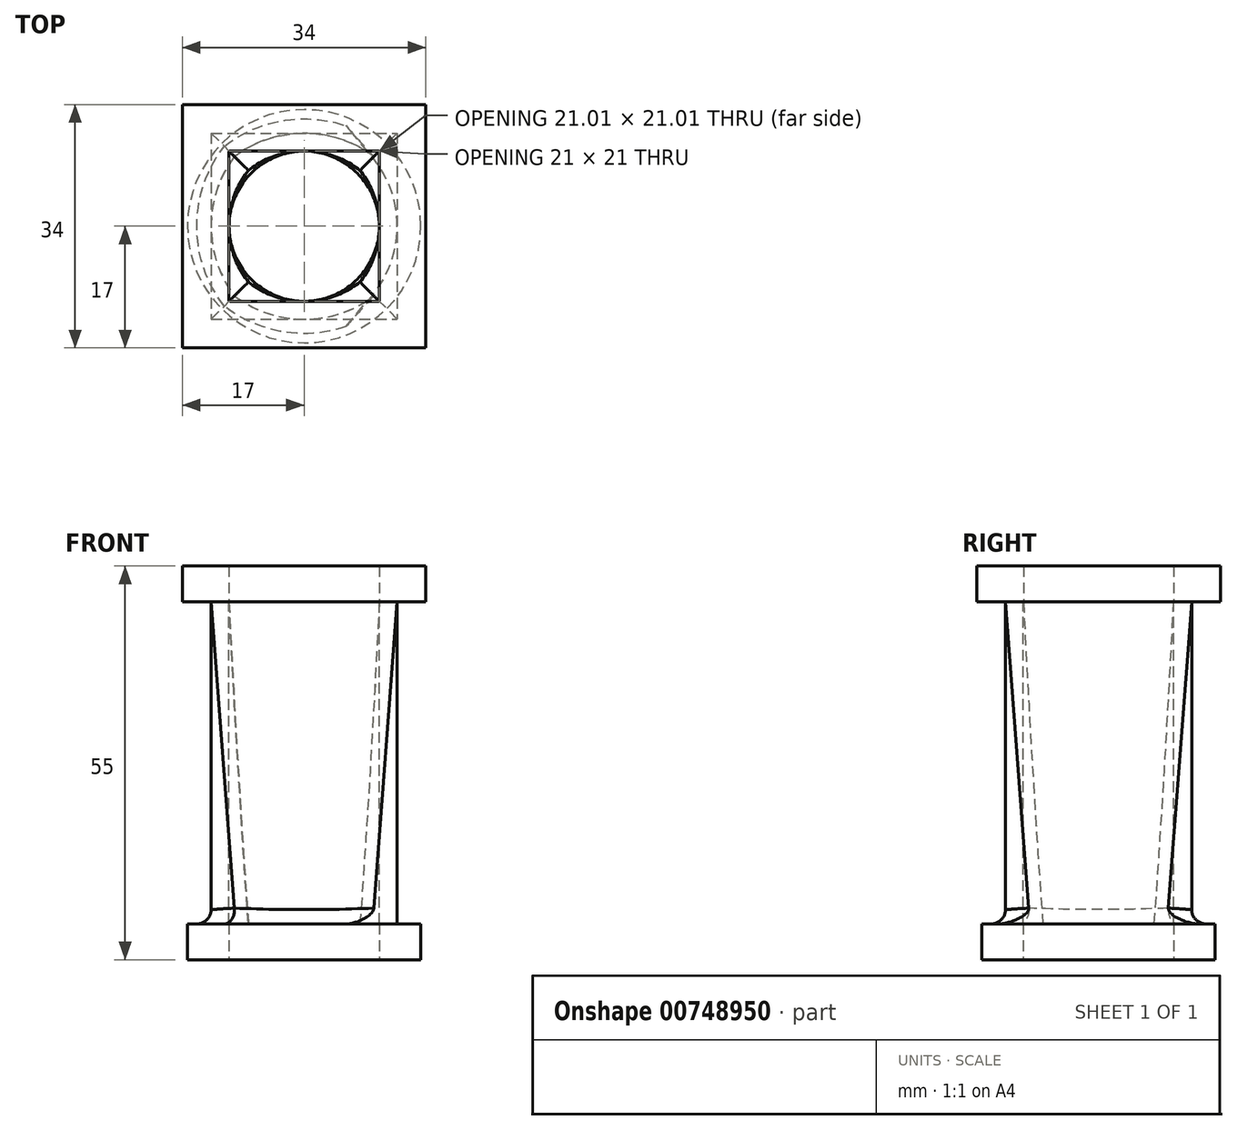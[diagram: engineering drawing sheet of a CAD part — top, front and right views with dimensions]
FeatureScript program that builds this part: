
annotation { "Feature Type Name" : "Feature", "Feature Type Description" : "" }
export const myFeature = defineFeature(function(context is Context, id is Id, definition is map)
    precondition{}
    {
        {
            var Q0;
            Q0=qCreatedBy(makeId("Top.planeOp"),FACE);
            var sketch = newSketch(context, id + "F0", { "sketchPlane" : qUnion([Q0])});
            skCircle(sketch, "E0", {"center": v(0, 0) * mm, "radius": 25 * mm});
            skCircle(sketch, "E1", {"center": v(0, 18) * mm, "radius": 2.5 * mm, "construction": true});
            skCircle(sketch, "E2", {"center": v(0, 0) * mm, "radius": 20.5 * mm});
            skCircle(sketch, "E3.1.0", {"center": v(-15.59, -9) * mm, "radius": 2.5 * mm, "construction": true});
            skCircle(sketch, "E3.2.0", {"center": v(15.59, -9) * mm, "radius": 2.5 * mm, "construction": true});
            skCircle(sketch, "E4", {"center": v(0, 0) * mm, "radius": 13 * mm});
            skSolve(sketch);
        }
        {
            var Q0;
            Q0=qCreatedBy(makeId("Top.planeOp"),FACE);
            cPlane(context, id + "F1", {"entities" : qUnion([Q0]), "cplaneType" : CPlaneType.OFFSET, "offset" : 50 * mm, "width" : 150 * mm, "height" : 150 * mm});
        }
        {
            var Q0;
            Q0=qCreatedBy(id+"F1.planeOp",FACE);
            var sketch = newSketch(context, id + "F2", { "sketchPlane" : qUnion([Q0])});
            skLineSegment(sketch, "E5.bottom", {"start": v(25, 25) * mm, "end": v(-25, 25) * mm});
            skLineSegment(sketch, "E5.top", {"start": v(25, -25) * mm, "end": v(-25, -25) * mm});
            skLineSegment(sketch, "E5.left", {"start": v(25, 25) * mm, "end": v(25, -25) * mm});
            skLineSegment(sketch, "E5.right", {"start": v(-25, 25) * mm, "end": v(-25, -25) * mm});
            skPoint(sketch, "E5.middle", {"position": v(0, 0) * mm});
            skPoint(sketch, "E6", {"position": v(0, 25) * mm});
            skLineSegment(sketch, "E7.bottom", {"start": v(18, 18) * mm, "end": v(-18, 18) * mm});
            skLineSegment(sketch, "E7.top", {"start": v(18, -18) * mm, "end": v(-18, -18) * mm});
            skLineSegment(sketch, "E7.left", {"start": v(18, 18) * mm, "end": v(18, -18) * mm});
            skLineSegment(sketch, "E7.right", {"start": v(-18, 18) * mm, "end": v(-18, -18) * mm});
            skLineSegment(sketch, "E8.bottom", {"start": v(-13, 13) * mm, "end": v(13, 13) * mm});
            skLineSegment(sketch, "E8.top", {"start": v(-13, -13) * mm, "end": v(13, -13) * mm});
            skLineSegment(sketch, "E8.left", {"start": v(-13, 13) * mm, "end": v(-13, -13) * mm});
            skLineSegment(sketch, "E8.right", {"start": v(13, 13) * mm, "end": v(13, -13) * mm});
            skSolve(sketch);
        }
        {
            var Q0;
            Q0=makeQuery(id+"F2.imprint","IMPRINT",FACE,{"disambiguationData":[TD([[makeQuery(id+"F2.imprint","IMPRINT",EDGE,{"derivedFrom":sQuery(id+"F2.wireOp",EDGE,"E8.bottom")}),-1.0]])]});
            var Q1;
            Q1=makeQuery(id+"F0.imprint","IMPRINT",FACE,{"disambiguationData":[TD([[makeQuery(id+"F0.imprint","IMPRINT",EDGE,{"derivedFrom":sQuery(id+"F0.wireOp",EDGE,"E4")}),1.0]])]});
            loft(context, id + "F3", {"sheetProfilesArray" : [{ "sheetProfileEntities" : qUnion([Q0]) }, { "sheetProfileEntities" : qUnion([Q1]) }]});
        }
        {
            var Q0;
            Q0=makeQuery(id+"F3.opLoft","CAP_FACE",FACE,{"disambiguationData":[OSD([makeQuery(id+"F0.imprint","IMPRINT",FACE,{"disambiguationData":[TD([[makeQuery(id+"F0.imprint","IMPRINT",EDGE,{"derivedFrom":sQuery(id+"F0.wireOp",EDGE,"E4")}),1.0]])]})])],"isStart":true});
            var Q1;
            Q1=makeQuery(id+"F3.opLoft","CAP_FACE",FACE,{"disambiguationData":[OSD([makeQuery(id+"F2.imprint","IMPRINT",FACE,{"disambiguationData":[TD([[makeQuery(id+"F2.imprint","IMPRINT",EDGE,{"derivedFrom":sQuery(id+"F2.wireOp",EDGE,"E8.bottom")}),-1.0]])]})])],"isStart":true});
            shell(context, id + "F4", {"entities" : qUnion([Q0, Q1]), "thickness" : 2.5 * mm});
        }
        {
            var Q0;
            Q0=makeQuery(id+"F3.opLoft","CAP_FACE",FACE,{"disambiguationData":[OSD([makeQuery(id+"F0.imprint","IMPRINT",FACE,{"disambiguationData":[TD([[makeQuery(id+"F0.imprint","IMPRINT",EDGE,{"derivedFrom":sQuery(id+"F0.wireOp",EDGE,"E4")}),1.0]])]})])],"isStart":true});
            var sketch = newSketch(context, id + "F5", { "sketchPlane" : qUnion([Q0])});
            skCircle(sketch, "E9", {"center": v(0, 0) * mm, "radius": 16.3 * mm});
            skSolve(sketch);
        }
        {
            var Q0;
            Q0=makeQuery(id+"F5.imprint","IMPRINT",FACE,{"disambiguationData":[TD([[makeQuery(id+"F5.imprint","IMPRINT",EDGE,{"derivedFrom":sQuery(id+"F5.wireOp",EDGE,"E9")}),1.0]])]});
            var Q1;
            {var subQ2=sQuery(id+"F2.wireOp",EDGE,"E8.bottom");var subQ3=sQuery(id+"F0.wireOp",EDGE,"E4");var subQ5=sQuery(id+"F2.wireOp",EDGE,"E8.left");Q1=makeQuery(id+"F5.imprint","IMPRINT",FACE,{"disambiguationData":[TD([[makeQuery(id+"F5.imprint","IMPRINT",EDGE,{"derivedFrom":makeQuery(id+"F3.opLoft","MID_CAP_EDGE",EDGE,{"disambiguationData":[OSD([subQ3,subQ2,subQ5])],"capPos":1.0})}),1.0]])]});}
            extrude(context, id + "F6", {"entities" : qUnion([Q0, Q1]), "operationType" : NewBodyOperationType.ADD, "oppositeDirection" : true, "depth" : 5 * mm, "offsetDistance" : 25 * mm});
        }
        {
            var Q0;
            Q0=makeQuery(id+"F3.opLoft","CAP_FACE",FACE,{"disambiguationData":[OSD([makeQuery(id+"F2.imprint","IMPRINT",FACE,{"disambiguationData":[TD([[makeQuery(id+"F2.imprint","IMPRINT",EDGE,{"derivedFrom":sQuery(id+"F2.wireOp",EDGE,"E8.bottom")}),-1.0]])]})])],"isStart":true});
            var sketch = newSketch(context, id + "F7", { "sketchPlane" : qUnion([Q0])});
            skLineSegment(sketch, "E10.bottom", {"start": v(-17, 17) * mm, "end": v(17, 17) * mm});
            skLineSegment(sketch, "E10.top", {"start": v(-17, -17) * mm, "end": v(17, -17) * mm});
            skLineSegment(sketch, "E10.left", {"start": v(-17, 17) * mm, "end": v(-17, -17) * mm});
            skLineSegment(sketch, "E10.right", {"start": v(17, 17) * mm, "end": v(17, -17) * mm});
            skPoint(sketch, "E10.middle", {"position": v(0, 0) * mm});
            skSolve(sketch);
        }
        {
            var Q0;
            Q0=makeQuery(id+"F7.imprint","IMPRINT",FACE,{"disambiguationData":[TD([[makeQuery(id+"F7.imprint","IMPRINT",EDGE,{"derivedFrom":sQuery(id+"F7.wireOp",EDGE,"E10.bottom")}),-1.0]])]});
            var Q1;
            {var subQ0=sQuery(id+"F2.wireOp",EDGE,"E8.right");var subQ1=sQuery(id+"F2.wireOp",EDGE,"E8.left");var subQ3=sQuery(id+"F2.wireOp",EDGE,"E8.bottom");Q1=makeQuery(id+"F7.imprint","IMPRINT",FACE,{"disambiguationData":[TD([[makeQuery(id+"F7.imprint","IMPRINT",EDGE,{"derivedFrom":makeQuery(id+"F3.opLoft","MID_CAP_EDGE",EDGE,{"disambiguationData":[OSD([subQ3,subQ1,subQ0])],"capPos":0.0})}),-1.0]])]});}
            extrude(context, id + "F8", {"entities" : qUnion([Q0, Q1]), "depth" : 5 * mm, "offsetDistance" : 25 * mm});
        }
        {
            var Q0;
            {var subQ0=sQuery(id+"F2.wireOp",EDGE,"E8.right");var subQ1=sQuery(id+"F2.wireOp",EDGE,"E8.left");var subQ2=sQuery(id+"F2.wireOp",EDGE,"E8.top");var subQ3=sQuery(id+"F2.wireOp",EDGE,"E8.bottom");var subQ4=sQuery(id+"F0.wireOp",EDGE,"E4");Q0=makeQuery(id+"F6.boolean.opBoolean","INTERSECT",EDGE,{"derivedFrom":[makeQuery(id+"F3.opLoft","SWEPT_FACE",FACE,{"disambiguationData":[OSD([subQ4,subQ3,subQ2,subQ1,subQ0]),TDD([makeQuery(id+"F0.imprint","IMPRINT",EDGE,{"derivedFrom":subQ4}),makeQuery(id+"F2.imprint","INTERSECT",VERTEX,{"derivedFrom":[subQ3,subQ1]}),makeQuery(id+"F2.imprint","INTERSECT",VERTEX,{"derivedFrom":[subQ3,subQ0]}),makeQuery(id+"F2.imprint","INTERSECT",VERTEX,{"derivedFrom":[subQ2,subQ0]}),makeQuery(id+"F2.imprint","IMPRINT",EDGE,{"derivedFrom":subQ0})])]}),makeQuery(id+"F6.opExtrude","CAP_FACE",FACE,{"disambiguationData":[OSD([subQ4,subQ3,subQ2,subQ1,subQ0,sQuery(id+"F5.wireOp",EDGE,"E9")])],"isStart":false})]});}
            var Q1;
            {var subQ0=sQuery(id+"F2.wireOp",EDGE,"E8.right");var subQ1=sQuery(id+"F2.wireOp",EDGE,"E8.left");var subQ2=sQuery(id+"F2.wireOp",EDGE,"E8.top");var subQ3=sQuery(id+"F2.wireOp",EDGE,"E8.bottom");var subQ4=sQuery(id+"F0.wireOp",EDGE,"E4");Q1=makeQuery(id+"F6.boolean.opBoolean","INTERSECT",EDGE,{"derivedFrom":[makeQuery(id+"F3.opLoft","SWEPT_FACE",FACE,{"disambiguationData":[OSD([subQ4,subQ3,subQ2,subQ1,subQ0]),TDD([makeQuery(id+"F0.imprint","IMPRINT",EDGE,{"derivedFrom":subQ4}),makeQuery(id+"F2.imprint","INTERSECT",VERTEX,{"derivedFrom":[subQ3,subQ1]}),makeQuery(id+"F2.imprint","INTERSECT",VERTEX,{"derivedFrom":[subQ2,subQ1]}),makeQuery(id+"F2.imprint","INTERSECT",VERTEX,{"derivedFrom":[subQ2,subQ0]}),makeQuery(id+"F2.imprint","IMPRINT",EDGE,{"derivedFrom":subQ1})])]}),makeQuery(id+"F6.opExtrude","CAP_FACE",FACE,{"disambiguationData":[OSD([subQ4,subQ3,subQ2,subQ1,subQ0,sQuery(id+"F5.wireOp",EDGE,"E9")])],"isStart":false})]});}
            var Q2;
            {var subQ0=sQuery(id+"F2.wireOp",EDGE,"E8.right");var subQ1=sQuery(id+"F2.wireOp",EDGE,"E8.left");var subQ2=sQuery(id+"F2.wireOp",EDGE,"E8.top");var subQ3=sQuery(id+"F2.wireOp",EDGE,"E8.bottom");var subQ4=sQuery(id+"F0.wireOp",EDGE,"E4");Q2=makeQuery(id+"F6.boolean.opBoolean","INTERSECT",EDGE,{"derivedFrom":[makeQuery(id+"F3.opLoft","SWEPT_FACE",FACE,{"disambiguationData":[OSD([subQ4,subQ3,subQ2,subQ1,subQ0]),TDD([makeQuery(id+"F0.imprint","IMPRINT",EDGE,{"derivedFrom":subQ4}),makeQuery(id+"F2.imprint","INTERSECT",VERTEX,{"derivedFrom":[subQ3,subQ0]}),makeQuery(id+"F2.imprint","INTERSECT",VERTEX,{"derivedFrom":[subQ2,subQ1]}),makeQuery(id+"F2.imprint","INTERSECT",VERTEX,{"derivedFrom":[subQ2,subQ0]}),makeQuery(id+"F2.imprint","IMPRINT",EDGE,{"derivedFrom":subQ2})])]}),makeQuery(id+"F6.opExtrude","CAP_FACE",FACE,{"disambiguationData":[OSD([subQ4,subQ3,subQ2,subQ1,subQ0,sQuery(id+"F5.wireOp",EDGE,"E9")])],"isStart":false})]});}
            var Q3;
            {var subQ0=sQuery(id+"F2.wireOp",EDGE,"E8.right");var subQ1=sQuery(id+"F2.wireOp",EDGE,"E8.left");var subQ2=sQuery(id+"F2.wireOp",EDGE,"E8.bottom");var subQ3=sQuery(id+"F0.wireOp",EDGE,"E4");Q3=makeQuery(id+"F6.boolean.opBoolean","INTERSECT",EDGE,{"derivedFrom":[makeQuery(id+"F3.opLoft","SWEPT_FACE",FACE,{"disambiguationData":[OSD([subQ3,subQ2,subQ1,subQ0])]}),makeQuery(id+"F6.opExtrude","CAP_FACE",FACE,{"disambiguationData":[OSD([subQ3,subQ2,sQuery(id+"F2.wireOp",EDGE,"E8.top"),subQ1,subQ0,sQuery(id+"F5.wireOp",EDGE,"E9")])],"isStart":false})]});}
            fillet(context, id + "F9", {"entities" : qUnion([Q0, Q1, Q2, Q3]), "tangentPropagation" : true, "radius" : 2 * mm, "defaultsChanged" : false, "vertexSettings" : [], "allowEdgeOverflow" : false});
        }
    });
